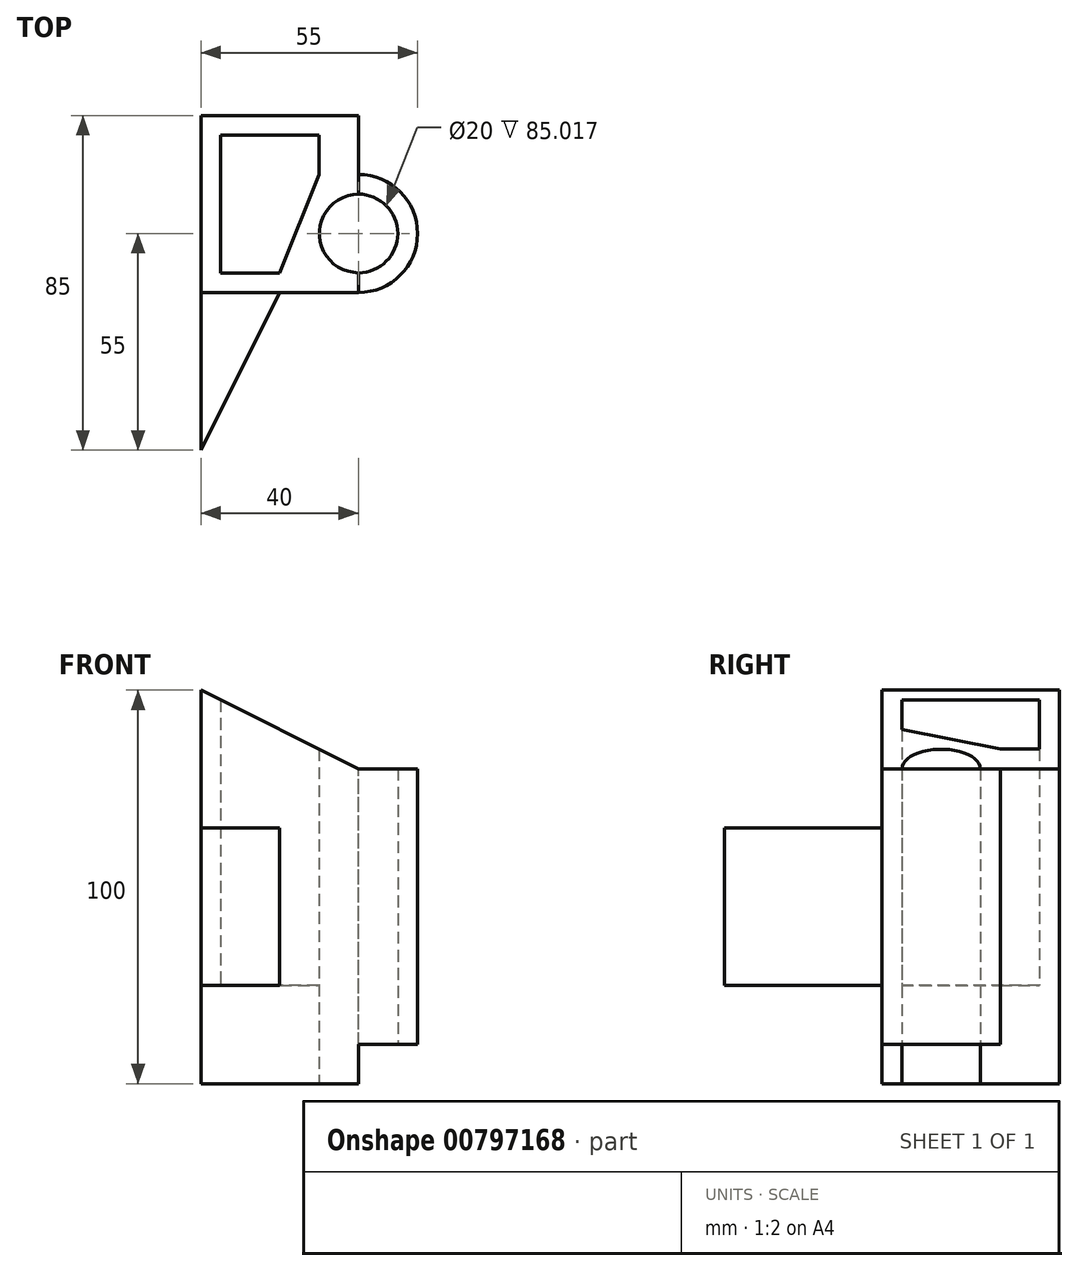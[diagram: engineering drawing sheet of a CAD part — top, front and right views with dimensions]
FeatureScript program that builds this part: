
annotation { "Feature Type Name" : "Feature", "Feature Type Description" : "" }
export const myFeature = defineFeature(function(context is Context, id is Id, definition is map)
    precondition{}
    {
        {
            var Q0;
            Q0=qCreatedBy(makeId("Front.planeOp"),FACE);
            var sketch = newSketch(context, id + "F0", { "sketchPlane" : qUnion([Q0])});
            skLineSegment(sketch, "E0.bottom", {"start": v(0, 0) * mm, "end": v(40, 0) * mm});
            skLineSegment(sketch, "E0.top", {"start": v(0, 100) * mm, "end": v(40, 100) * mm});
            skLineSegment(sketch, "E0.left", {"start": v(0, 0) * mm, "end": v(0, 100) * mm});
            skLineSegment(sketch, "E0.right", {"start": v(40, 0) * mm, "end": v(40, 100) * mm});
            skSolve(sketch);
        }
        {
            var Q0;
            Q0 = qSketchRegion(id + "F0", true);
            extrude(context, id + "F1", {"entities" : qUnion([Q0]), "oppositeDirection" : true, "depth" : 45 * mm, "offsetDistance" : 25 * mm});
        }
        {
            var Q0;
            Q0=makeQuery(id+"F1.opExtrude","SWEPT_FACE",FACE,{"disambiguationData":[OSD([sQuery(id+"F0.wireOp",EDGE,"E0.top")])]});
            var sketch = newSketch(context, id + "F2", { "sketchPlane" : qUnion([Q0])});
            skCircle(sketch, "E1", {"center": v(40, 15) * mm, "radius": 15 * mm});
            skSolve(sketch);
        }
        {
            var Q0;
            Q0 = qSketchRegion(id + "F2", true);
            extrude(context, id + "F3", {"entities" : qUnion([Q0]), "operationType" : NewBodyOperationType.ADD, "oppositeDirection" : true, "depth" : 90 * mm, "offsetDistance" : 25 * mm});
        }
        {
            var Q0;
            Q0=makeQuery(id+"F1.opExtrude","CAP_FACE",FACE,{"disambiguationData":[OSD([sQuery(id+"F0.wireOp",EDGE,"E0.bottom"),sQuery(id+"F0.wireOp",EDGE,"E0.top"),sQuery(id+"F0.wireOp",EDGE,"E0.left"),sQuery(id+"F0.wireOp",EDGE,"E0.right")])],"isStart":true});
            var sketch = newSketch(context, id + "F4", { "sketchPlane" : qUnion([Q0])});
            skLineSegment(sketch, "E2", {"start": v(0, 100) * mm, "end": v(40, 80) * mm});
            skLineSegment(sketch, "E3", {"start": v(40, 80) * mm, "end": v(62.43, 80) * mm});
            skLineSegment(sketch, "E4", {"start": v(62.43, 80) * mm, "end": v(62.43, 100) * mm});
            skLineSegment(sketch, "E5", {"start": v(62.43, 100) * mm, "end": v(0, 100) * mm});
            skSolve(sketch);
        }
        {
            var Q0;
            Q0 = qSketchRegion(id + "F4", true);
            extrude(context, id + "F5", {"entities" : qUnion([Q0]), "operationType" : NewBodyOperationType.REMOVE, "endBound" : BoundingType.THROUGH_ALL, "oppositeDirection" : true, "depth" : 25 * mm, "offsetDistance" : 25 * mm});
        }
        {
            var Q0;
            Q0=qCreatedBy(makeId("Top.planeOp"),FACE);
            var sketch = newSketch(context, id + "F6", { "sketchPlane" : qUnion([Q0])});
            skLineSegment(sketch, "E6", {"start": v(5, 40) * mm, "end": v(5, 5) * mm});
            skLineSegment(sketch, "E7", {"start": v(5, 5) * mm, "end": v(20, 5) * mm});
            skLineSegment(sketch, "E8", {"start": v(20, 5) * mm, "end": v(30, 30) * mm});
            skLineSegment(sketch, "E9", {"start": v(30, 30) * mm, "end": v(30, 40) * mm});
            skLineSegment(sketch, "E10", {"start": v(30, 40) * mm, "end": v(5, 40) * mm});
            skSolve(sketch);
        }
        {
            var Q0;
            Q0 = qSketchRegion(id + "F6", true);
            extrude(context, id + "F7", {"entities" : qUnion([Q0]), "operationType" : NewBodyOperationType.REMOVE, "endBound" : BoundingType.THROUGH_ALL, "depth" : 25 * mm, "offsetDistance" : 25 * mm});
        }
        {
            var Q0;
            Q0=makeQuery(id+"F1.opExtrude","SWEPT_FACE",FACE,{"disambiguationData":[OSD([sQuery(id+"F0.wireOp",EDGE,"E0.bottom")])]});
            var sketch = newSketch(context, id + "F8", { "sketchPlane" : qUnion([Q0])});
            skLineSegment(sketch, "E11.0", {"start": v(5, -40) * mm, "end": v(5, -5) * mm});
            skLineSegment(sketch, "E11.1", {"start": v(5, -5) * mm, "end": v(20, -5) * mm});
            skLineSegment(sketch, "E11.2", {"start": v(20, -5) * mm, "end": v(30, -30) * mm});
            skLineSegment(sketch, "E11.3", {"start": v(30, -30) * mm, "end": v(30, -40) * mm});
            skLineSegment(sketch, "E11.4", {"start": v(30, -40) * mm, "end": v(5, -40) * mm});
            skSolve(sketch);
        }
        {
            var Q0;
            Q0 = qSketchRegion(id + "F8", true);
            extrude(context, id + "F9", {"entities" : qUnion([Q0]), "operationType" : NewBodyOperationType.ADD, "oppositeDirection" : true, "depth" : 25 * mm, "offsetDistance" : 25 * mm});
        }
        {
            var Q0;
            Q0=qCreatedBy(makeId("Top.planeOp"),FACE);
            var sketch = newSketch(context, id + "F10", { "sketchPlane" : qUnion([Q0])});
            skCircle(sketch, "E12", {"center": v(40, 15) * mm, "radius": 10 * mm});
            skSolve(sketch);
        }
        {
            var Q0;
            Q0 = qSketchRegion(id + "F10", true);
            extrude(context, id + "F11", {"entities" : qUnion([Q0]), "operationType" : NewBodyOperationType.REMOVE, "endBound" : BoundingType.THROUGH_ALL, "depth" : 25 * mm, "offsetDistance" : 25 * mm});
        }
        {
            var Q0;
            Q0=qCreatedBy(makeId("Top.planeOp"),FACE);
            cPlane(context, id + "F12", {"entities" : qUnion([Q0]), "cplaneType" : CPlaneType.OFFSET, "offset" : 25 * mm, "width" : 150 * mm, "height" : 150 * mm});
        }
        {
            var Q0;
            Q0=qCreatedBy(id+"F12.planeOp",FACE);
            var sketch = newSketch(context, id + "F13", { "sketchPlane" : qUnion([Q0])});
            skLineSegment(sketch, "E13", {"start": v(0, 0) * mm, "end": v(0, -40) * mm});
            skLineSegment(sketch, "E14", {"start": v(0, -40) * mm, "end": v(20, 0) * mm});
            skLineSegment(sketch, "E15", {"start": v(20, 0) * mm, "end": v(0, 0) * mm});
            skSolve(sketch);
        }
        {
            var Q0;
            Q0 = qSketchRegion(id + "F13", true);
            extrude(context, id + "F14", {"entities" : qUnion([Q0]), "operationType" : NewBodyOperationType.ADD, "depth" : (40) * mm, "offsetDistance" : 25 * mm});
        }
    });
